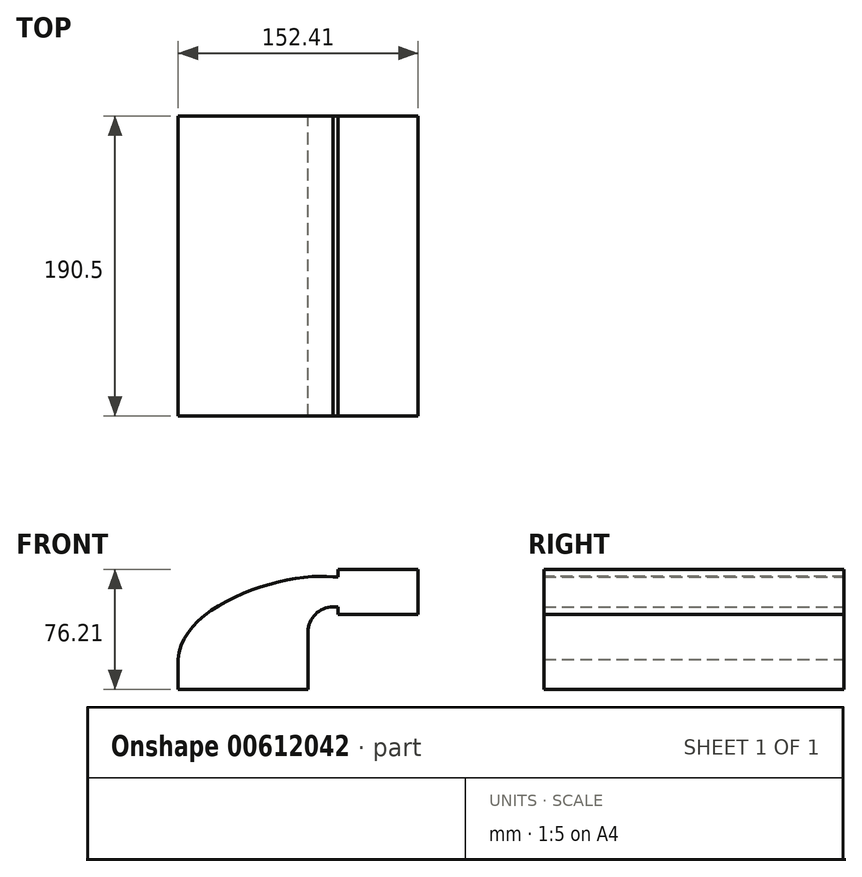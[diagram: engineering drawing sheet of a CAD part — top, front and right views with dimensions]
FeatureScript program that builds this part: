
annotation { "Feature Type Name" : "Feature", "Feature Type Description" : "" }
export const myFeature = defineFeature(function(context is Context, id is Id, definition is map)
    precondition{}
    {
        {
            var Q0;
            Q0=qCreatedBy(makeId("Front.planeOp"),FACE);
            var sketch = newSketch(context, id + "F0", { "sketchPlane" : qUnion([Q0])});
            skLineSegment(sketch, "E0.bottom", {"start": v(41.27, 9.53) * mm, "end": v(-41.28, 9.53) * mm});
            skLineSegment(sketch, "E0.top", {"start": v(41.28, -9.52) * mm, "end": v(-41.27, -9.52) * mm});
            skLineSegment(sketch, "E0.left", {"start": v(41.28, 9.53) * mm, "end": v(41.28, -9.52) * mm});
            skLineSegment(sketch, "E0.right", {"start": v(-41.28, 9.53) * mm, "end": v(-41.28, -9.52) * mm});
            skPoint(sketch, "E0.middle", {"position": v(0, 0) * mm});
            skLineSegment(sketch, "E1.bottom", {"start": v(60.32, 38.1) * mm, "end": v(111.12, 38.1) * mm});
            skLineSegment(sketch, "E1.top", {"start": v(60.32, 66.68) * mm, "end": v(111.12, 66.68) * mm});
            skLineSegment(sketch, "E1.left", {"start": v(60.32, 38.1) * mm, "end": v(60.32, 66.68) * mm});
            skLineSegment(sketch, "E1.right", {"start": v(111.12, 38.1) * mm, "end": v(111.12, 66.68) * mm});
            skPoint(sketch, "E1.middle", {"position": v(85.72, 52.39) * mm});
            skLineSegment(sketch, "E2", {"start": v(41.27, 9.53) * mm, "end": v(41.27, 27) * mm});
            skArc(sketch, "E3", {"start": v(41.27, 27) * mm, "mid": v(45.92, 38.23) * mm, "end": v(57.15, 42.88) * mm});
            skLineSegment(sketch, "E4", {"start": v(57.15, 42.88) * mm, "end": v(85.72, 42.88) * mm});
            skPoint(sketch, "E5", {"position": v(85.72, 38.1) * mm});
            skLineSegment(sketch, "E6.0", {"start": v(57.15, 61.93) * mm, "end": v(85.72, 61.93) * mm});
            skArc(sketch, "E6.1", {"start": v(22.22, 27) * mm, "mid": v(32.45, 51.7) * mm, "end": v(57.15, 61.93) * mm});
            skLineSegment(sketch, "E6.2", {"start": v(22.22, 9.53) * mm, "end": v(22.22, 27) * mm});
            skLineSegment(sketch, "E7", {"start": v(85.72, 52.39) * mm, "end": v(85.72, 66.68) * mm});
            skFitSpline(sketch, "E8", {"points": [v(-41.27, 9.52) * mm, v(57.15, 61.93) * mm], "startDerivative": vector(4.85, 105.35) * mm, "endDerivative": vector(90.64, -11.18) * mm});
            skSolve(sketch);
        }
        {
            var Q0;
            Q0 = qSketchRegion(id + "F0", true);
            extrude(context, id + "F1", {"entities" : qUnion([Q0]), "endBound" : BoundingType.SYMMETRIC, "depth" : 127 * mm, "offsetDistance" : 25.4 * mm});
        }
        {
            var Q0;
            Q0=makeQuery(id+"F1.opExtrude","CAP_FACE",FACE,{"disambiguationData":[OSD([sQuery(id+"F0.wireOp",EDGE,"E0.top"),sQuery(id+"F0.wireOp",EDGE,"E0.left"),sQuery(id+"F0.wireOp",EDGE,"E0.right"),sQuery(id+"F0.wireOp",EDGE,"E1.bottom"),sQuery(id+"F0.wireOp",EDGE,"E1.top"),sQuery(id+"F0.wireOp",EDGE,"E1.left"),sQuery(id+"F0.wireOp",EDGE,"E1.right"),sQuery(id+"F0.wireOp",EDGE,"E2"),sQuery(id+"F0.wireOp",EDGE,"E3"),sQuery(id+"F0.wireOp",EDGE,"E4"),sQuery(id+"F0.wireOp",EDGE,"E6.0"),sQuery(id+"F0.wireOp",EDGE,"E8")])],"isStart":false});
            extrude(context, id + "F2", {"entities" : qUnion([Q0]), "operationType" : NewBodyOperationType.ADD, "endBound" : BoundingType.SYMMETRIC, "depth" : 127 * mm, "offsetDistance" : 25.4 * mm});
        }
    });
